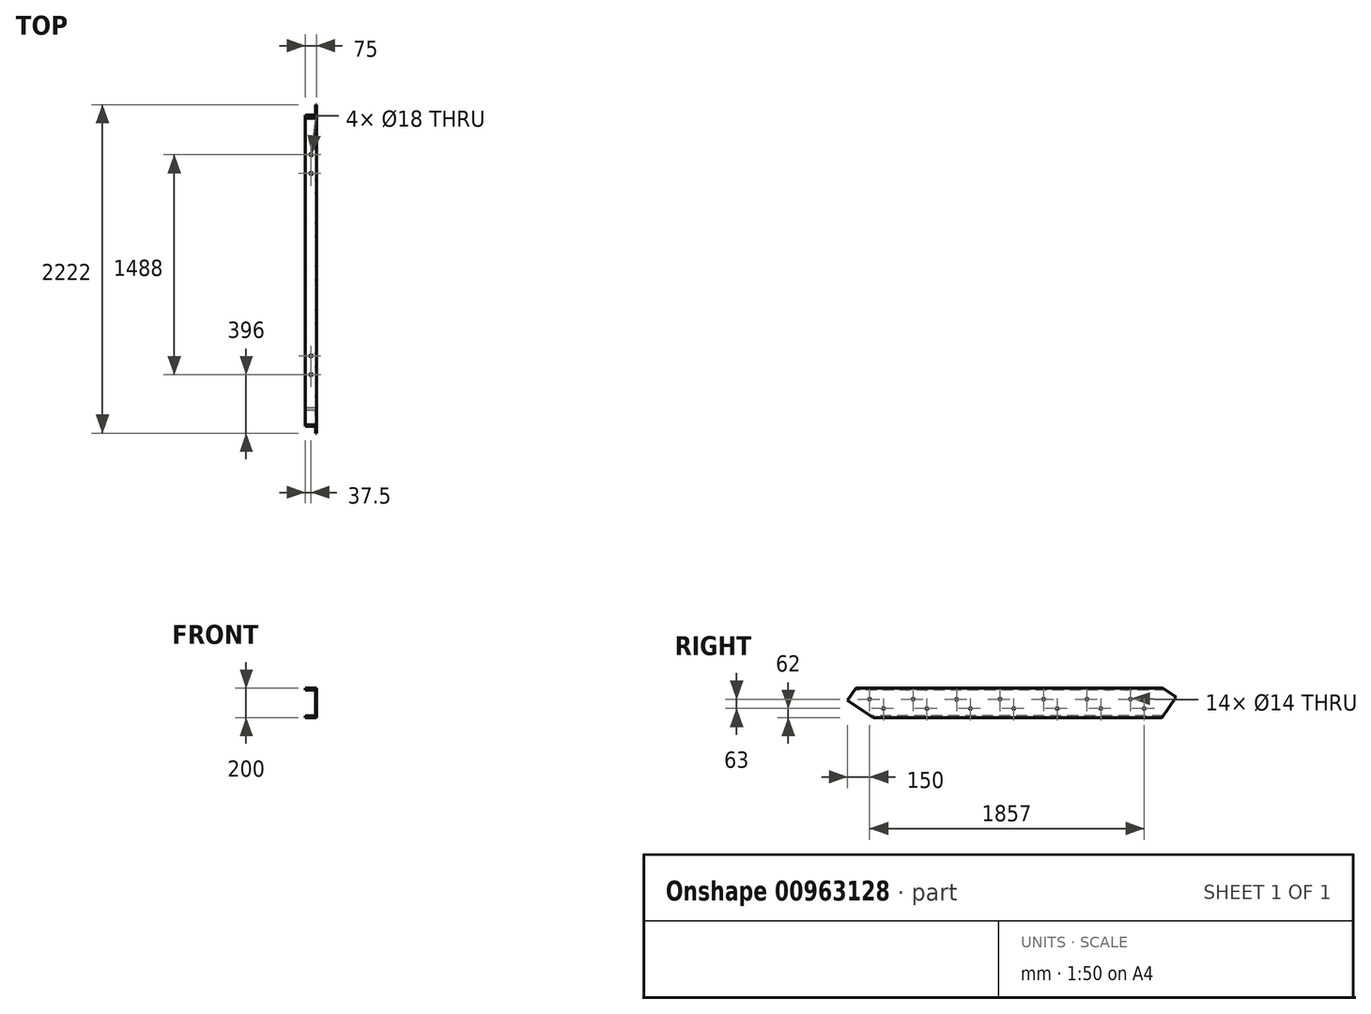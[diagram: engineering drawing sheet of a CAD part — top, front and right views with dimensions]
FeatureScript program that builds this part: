
annotation { "Feature Type Name" : "Feature", "Feature Type Description" : "" }
export const myFeature = defineFeature(function(context is Context, id is Id, definition is map)
    precondition{}
    {
        {
            var Q0;
            Q0=qCreatedBy(makeId("Front.planeOp"),FACE);
            var sketch = newSketch(context, id + "F0", { "sketchPlane" : qUnion([Q0])});
            skLineSegment(sketch, "E0", {"start": v(0, 0) * mm, "end": v(75, 0) * mm});
            skLineSegment(sketch, "E1", {"start": v(75, 0) * mm, "end": v(75, -200) * mm});
            skLineSegment(sketch, "E2", {"start": v(75, -200) * mm, "end": v(0, -200) * mm});
            skLineSegment(sketch, "E3.0", {"start": v(69, -24.5) * mm, "end": v(69, -175.5) * mm});
            skLineSegment(sketch, "E4.0", {"start": v(0, -12.5) * mm, "end": v(57, -12.5) * mm});
            skLineSegment(sketch, "E5.0", {"start": v(57, -187.5) * mm, "end": v(0, -187.5) * mm});
            skLineSegment(sketch, "E6", {"start": v(0, 0) * mm, "end": v(0, -12.5) * mm});
            skLineSegment(sketch, "E7", {"start": v(0, -187.5) * mm, "end": v(0, -200) * mm});
            skArc(sketch, "E8.filletArc", {"start": v(57, -187.5) * mm, "mid": v(65.49, -183.99) * mm, "end": v(69, -175.5) * mm});
            skArc(sketch, "E9.filletArc", {"start": v(69, -24.5) * mm, "mid": v(65.49, -16.01) * mm, "end": v(57, -12.5) * mm});
            skSolve(sketch);
        }
        {
            var Q0;
            Q0=makeQuery(id+"F0.imprint","IMPRINT",FACE,{"disambiguationData":[TD([[makeQuery(id+"F0.imprint","IMPRINT",EDGE,{"derivedFrom":sQuery(id+"F0.wireOp",EDGE,"E0")}),-1.0]])]});
            extrude(context, id + "F1", {"entities" : qUnion([Q0]), "oppositeDirection" : true, "depth" : 2222 * mm, "offsetDistance" : 25 * mm});
        }
        {
            var Q0;
            Q0=makeQuery(id+"F1.opExtrude","SWEPT_FACE",FACE,{"disambiguationData":[OSD([sQuery(id+"F0.wireOp",EDGE,"E1")])]});
            var sketch = newSketch(context, id + "F2", { "sketchPlane" : qUnion([Q0])});
            skLineSegment(sketch, "E10", {"start": v(0, 0) * mm, "end": v(0, -83) * mm});
            skLineSegment(sketch, "E11", {"start": v(0, 0) * mm, "end": v(56, 0) * mm});
            skLineSegment(sketch, "E12", {"start": v(56, 0) * mm, "end": v(0, -83) * mm});
            skLineSegment(sketch, "E13", {"start": v(0, -200) * mm, "end": v(174, -200) * mm});
            skLineSegment(sketch, "E14", {"start": v(174, -200) * mm, "end": v(0, -83) * mm});
            skLineSegment(sketch, "E15", {"start": v(0, 0) * mm, "end": v(150, 0) * mm});
            skLineSegment(sketch, "E16", {"start": v(150, 0) * mm, "end": v(243, 0) * mm});
            skCircle(sketch, "E17", {"center": v(150, -75) * mm, "radius": 7 * mm});
            skCircle(sketch, "E18", {"center": v(243, -138) * mm, "radius": 7 * mm});
            skCircle(sketch, "E19.1.0.0", {"center": v(444, -75) * mm, "radius": 7 * mm});
            skCircle(sketch, "E19.1.0.1", {"center": v(537, -138) * mm, "radius": 7 * mm});
            skCircle(sketch, "E19.2.0.0", {"center": v(738, -75) * mm, "radius": 7 * mm});
            skCircle(sketch, "E19.2.0.1", {"center": v(831, -138) * mm, "radius": 7 * mm});
            skCircle(sketch, "E19.3.0.0", {"center": v(1032, -75) * mm, "radius": 7 * mm});
            skCircle(sketch, "E19.3.0.1", {"center": v(1125, -138) * mm, "radius": 7 * mm});
            skCircle(sketch, "E19.4.0.0", {"center": v(1326, -75) * mm, "radius": 7 * mm});
            skCircle(sketch, "E19.4.0.1", {"center": v(1419, -138) * mm, "radius": 7 * mm});
            skCircle(sketch, "E19.5.0.0", {"center": v(1620, -75) * mm, "radius": 7 * mm});
            skCircle(sketch, "E19.5.0.1", {"center": v(1713, -138) * mm, "radius": 7 * mm});
            skCircle(sketch, "E19.6.0.0", {"center": v(1914, -75) * mm, "radius": 7 * mm});
            skCircle(sketch, "E19.6.0.1", {"center": v(2007, -138) * mm, "radius": 7 * mm});
            skLineSegment(sketch, "E19.direction1", {"start": v(150, -75) * mm, "end": v(444, -75) * mm, "construction": true});
            skLineSegment(sketch, "E20", {"start": v(2222, 0) * mm, "end": v(2134, 0) * mm});
            skLineSegment(sketch, "E21", {"start": v(2222, 0) * mm, "end": v(2222, -59) * mm});
            skLineSegment(sketch, "E22", {"start": v(2222, -59) * mm, "end": v(2134, 0) * mm});
            skLineSegment(sketch, "E23", {"start": v(2222, -200) * mm, "end": v(2127, -200) * mm});
            skLineSegment(sketch, "E24", {"start": v(2127, -200) * mm, "end": v(2222, -59) * mm});
            skSolve(sketch);
        }
        {
            var Q0;
            {var subQ0=sQuery(id+"F2.wireOp",EDGE,"E13");Q0=makeQuery(id+"F2.imprint","IMPRINT",FACE,{"disambiguationData":[TD([[makeQuery(id+"F2.imprint","IMPRINT",EDGE,{"derivedFrom":subQ0}),-1.0]])]});}
            var Q1;
            {var subQ0=sQuery(id+"F2.wireOp",EDGE,"E10");Q1=makeQuery(id+"F2.imprint","IMPRINT",FACE,{"disambiguationData":[TD([[makeQuery(id+"F2.imprint","IMPRINT",EDGE,{"derivedFrom":subQ0}),1.0]])]});}
            var Q2;
            {var subQ0=sQuery(id+"F2.wireOp",EDGE,"E23");Q2=makeQuery(id+"F2.imprint","IMPRINT",FACE,{"disambiguationData":[TD([[makeQuery(id+"F2.imprint","IMPRINT",EDGE,{"derivedFrom":subQ0}),-1.0]])]});}
            var Q3;
            Q3=makeQuery(id+"F2.imprint","IMPRINT",FACE,{"disambiguationData":[TD([[makeQuery(id+"F2.imprint","IMPRINT",EDGE,{"derivedFrom":sQuery(id+"F2.wireOp",EDGE,"E20")}),1.0]])]});
            var Q4;
            Q4=makeQuery(id+"F2.imprint","IMPRINT",FACE,{"disambiguationData":[TD([[makeQuery(id+"F2.imprint","IMPRINT",EDGE,{"derivedFrom":sQuery(id+"F2.wireOp",EDGE,"E19.1.0.0")}),1.0]])]});
            var Q5;
            Q5=makeQuery(id+"F2.imprint","IMPRINT",FACE,{"disambiguationData":[TD([[makeQuery(id+"F2.imprint","IMPRINT",EDGE,{"derivedFrom":sQuery(id+"F2.wireOp",EDGE,"E19.1.0.1")}),1.0]])]});
            var Q6;
            Q6=makeQuery(id+"F2.imprint","IMPRINT",FACE,{"disambiguationData":[TD([[makeQuery(id+"F2.imprint","IMPRINT",EDGE,{"derivedFrom":sQuery(id+"F2.wireOp",EDGE,"E18")}),1.0]])]});
            var Q7;
            Q7=makeQuery(id+"F2.imprint","IMPRINT",FACE,{"disambiguationData":[TD([[makeQuery(id+"F2.imprint","IMPRINT",EDGE,{"derivedFrom":sQuery(id+"F2.wireOp",EDGE,"E17")}),1.0]])]});
            var Q8;
            Q8=makeQuery(id+"F2.imprint","IMPRINT",FACE,{"disambiguationData":[TD([[makeQuery(id+"F2.imprint","IMPRINT",EDGE,{"derivedFrom":sQuery(id+"F2.wireOp",EDGE,"E19.2.0.0")}),1.0]])]});
            var Q9;
            Q9=makeQuery(id+"F2.imprint","IMPRINT",FACE,{"disambiguationData":[TD([[makeQuery(id+"F2.imprint","IMPRINT",EDGE,{"derivedFrom":sQuery(id+"F2.wireOp",EDGE,"E19.2.0.1")}),1.0]])]});
            var Q10;
            Q10=makeQuery(id+"F2.imprint","IMPRINT",FACE,{"disambiguationData":[TD([[makeQuery(id+"F2.imprint","IMPRINT",EDGE,{"derivedFrom":sQuery(id+"F2.wireOp",EDGE,"E19.3.0.0")}),1.0]])]});
            var Q11;
            Q11=makeQuery(id+"F2.imprint","IMPRINT",FACE,{"disambiguationData":[TD([[makeQuery(id+"F2.imprint","IMPRINT",EDGE,{"derivedFrom":sQuery(id+"F2.wireOp",EDGE,"E19.3.0.1")}),1.0]])]});
            var Q12;
            Q12=makeQuery(id+"F2.imprint","IMPRINT",FACE,{"disambiguationData":[TD([[makeQuery(id+"F2.imprint","IMPRINT",EDGE,{"derivedFrom":sQuery(id+"F2.wireOp",EDGE,"E19.4.0.0")}),1.0]])]});
            var Q13;
            Q13=makeQuery(id+"F2.imprint","IMPRINT",FACE,{"disambiguationData":[TD([[makeQuery(id+"F2.imprint","IMPRINT",EDGE,{"derivedFrom":sQuery(id+"F2.wireOp",EDGE,"E19.4.0.1")}),1.0]])]});
            var Q14;
            Q14=makeQuery(id+"F2.imprint","IMPRINT",FACE,{"disambiguationData":[TD([[makeQuery(id+"F2.imprint","IMPRINT",EDGE,{"derivedFrom":sQuery(id+"F2.wireOp",EDGE,"E19.5.0.0")}),1.0]])]});
            var Q15;
            Q15=makeQuery(id+"F2.imprint","IMPRINT",FACE,{"disambiguationData":[TD([[makeQuery(id+"F2.imprint","IMPRINT",EDGE,{"derivedFrom":sQuery(id+"F2.wireOp",EDGE,"E19.5.0.1")}),1.0]])]});
            var Q16;
            Q16=makeQuery(id+"F2.imprint","IMPRINT",FACE,{"disambiguationData":[TD([[makeQuery(id+"F2.imprint","IMPRINT",EDGE,{"derivedFrom":sQuery(id+"F2.wireOp",EDGE,"E19.6.0.1")}),1.0]])]});
            var Q17;
            Q17=makeQuery(id+"F2.imprint","IMPRINT",FACE,{"disambiguationData":[TD([[makeQuery(id+"F2.imprint","IMPRINT",EDGE,{"derivedFrom":sQuery(id+"F2.wireOp",EDGE,"E19.6.0.0")}),1.0]])]});
            extrude(context, id + "F3", {"entities" : qUnion([Q0, Q1, Q2, Q3, Q4, Q5, Q6, Q7, Q8, Q9, Q10, Q11, Q12, Q13, Q14, Q15, Q16, Q17]), "operationType" : NewBodyOperationType.REMOVE, "endBound" : BoundingType.THROUGH_ALL, "oppositeDirection" : true, "depth" : 25 * mm, "offsetDistance" : 25 * mm});
        }
        {
            var Q0;
            Q0=makeQuery(id+"F1.opExtrude","SWEPT_FACE",FACE,{"disambiguationData":[OSD([sQuery(id+"F0.wireOp",EDGE,"E0")])]});
            var sketch = newSketch(context, id + "F4", { "sketchPlane" : qUnion([Q0])});
            skLineSegment(sketch, "E25", {"start": v(0, 56) * mm, "end": v(0, 396) * mm, "construction": true});
            skLineSegment(sketch, "E26", {"start": v(0, 396) * mm, "end": v(37.5, 396) * mm, "construction": true});
            skLineSegment(sketch, "E27", {"start": v(37.5, 396) * mm, "end": v(37.5, 441) * mm, "construction": true});
            skLineSegment(sketch, "E28", {"start": v(37.5, 441) * mm, "end": v(37.5, 523) * mm, "construction": true});
            skCircle(sketch, "E29", {"center": v(37.5, 523) * mm, "radius": 9 * mm});
            skCircle(sketch, "E30", {"center": v(37.5, 396) * mm, "radius": 9 * mm});
            skLineSegment(sketch, "E31", {"start": v(0, 2134) * mm, "end": v(0, 1884) * mm, "construction": true});
            skLineSegment(sketch, "E32", {"start": v(0, 1884) * mm, "end": v(37.5, 1884) * mm, "construction": true});
            skLineSegment(sketch, "E33", {"start": v(37.5, 1884) * mm, "end": v(37.5, 1839) * mm, "construction": true});
            skLineSegment(sketch, "E34", {"start": v(37.5, 1839) * mm, "end": v(37.5, 1757) * mm, "construction": true});
            skCircle(sketch, "E35", {"center": v(37.5, 1757) * mm, "radius": 9 * mm});
            skCircle(sketch, "E36", {"center": v(37.5, 1884) * mm, "radius": 9 * mm});
            skSolve(sketch);
        }
        {
            var Q0;
            Q0 = qSketchRegion(id + "F4", true);
            extrude(context, id + "F5", {"entities" : qUnion([Q0]), "operationType" : NewBodyOperationType.REMOVE, "oppositeDirection" : true, "depth" : 25 * mm, "offsetDistance" : 25 * mm});
        }
    });
